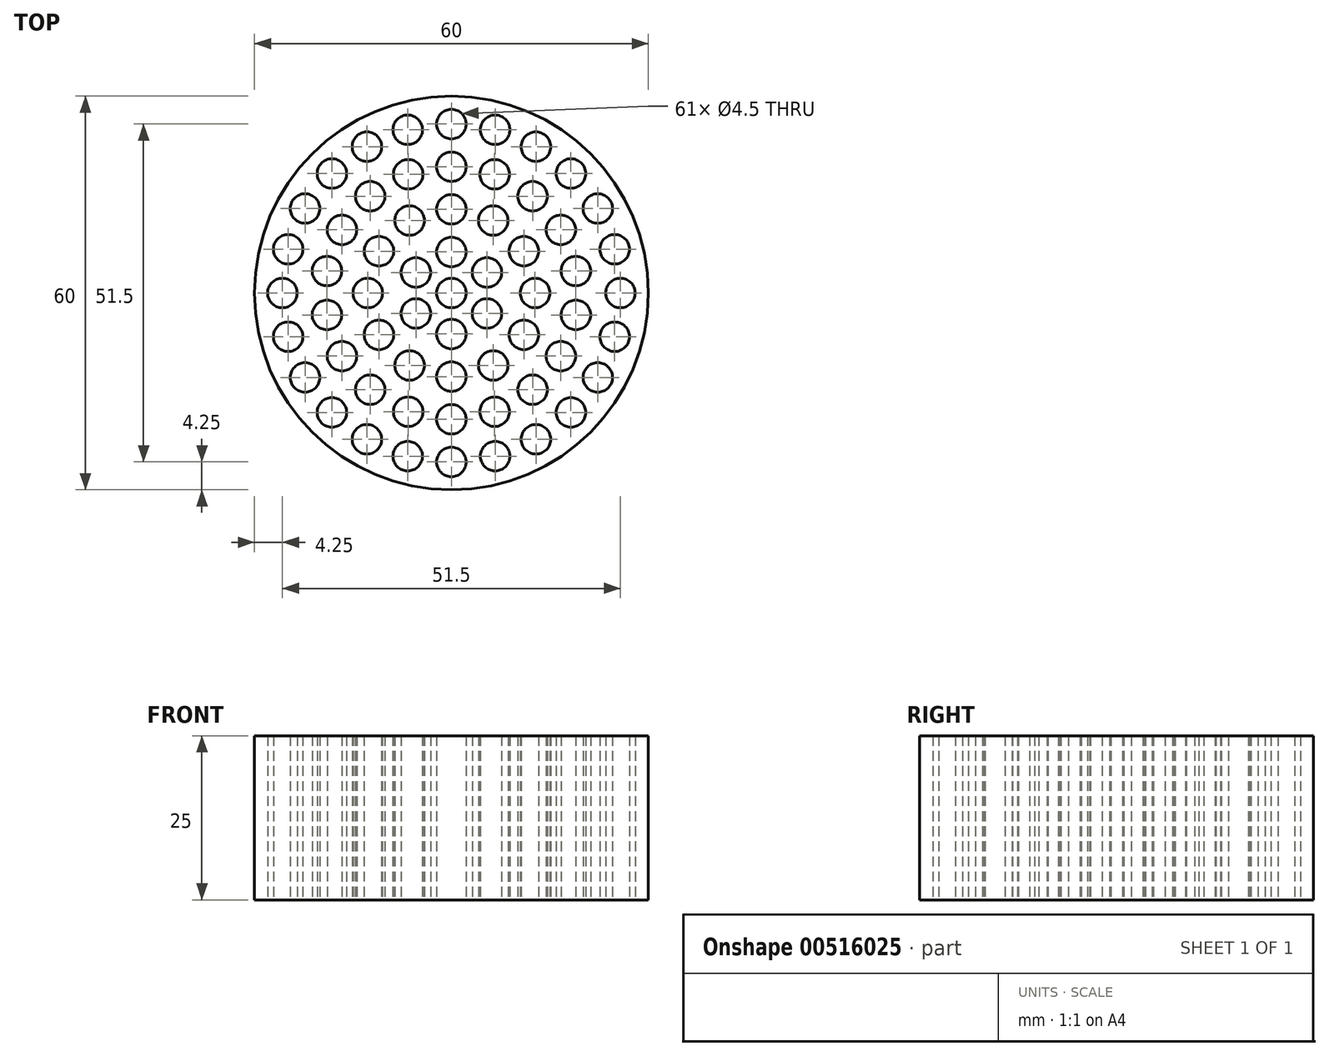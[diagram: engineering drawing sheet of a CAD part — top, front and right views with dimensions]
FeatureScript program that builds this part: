
annotation { "Feature Type Name" : "Feature", "Feature Type Description" : "" }
export const myFeature = defineFeature(function(context is Context, id is Id, definition is map)
    precondition{}
    {
        {
            var Q0;
            Q0=qCreatedBy(makeId("Top.planeOp"),FACE);
            var sketch = newSketch(context, id + "F0", { "sketchPlane" : qUnion([Q0])});
            skCircle(sketch, "E0", {"center": v(0, 0) * mm, "radius": 30 * mm});
            skLineSegment(sketch, "E1", {"start": v(0, 30) * mm, "end": v(0, -30) * mm});
            skCircle(sketch, "E2", {"center": v(0, 25.75) * mm, "radius": 2.25 * mm});
            skCircle(sketch, "E3.1.0", {"center": v(-6.66, 24.87) * mm, "radius": 2.25 * mm});
            skCircle(sketch, "E3.2.0", {"center": v(-12.87, 22.3) * mm, "radius": 2.25 * mm});
            skCircle(sketch, "E3.3.0", {"center": v(-18.2, 18.2) * mm, "radius": 2.25 * mm});
            skCircle(sketch, "E3.4.0", {"center": v(-22.3, 12.88) * mm, "radius": 2.25 * mm});
            skCircle(sketch, "E3.5.0", {"center": v(-24.87, 6.66) * mm, "radius": 2.25 * mm});
            skCircle(sketch, "E3.6.0", {"center": v(-25.75, 0) * mm, "radius": 2.25 * mm});
            skCircle(sketch, "E3.7.0", {"center": v(-24.87, -6.66) * mm, "radius": 2.25 * mm});
            skCircle(sketch, "E3.8.0", {"center": v(-22.3, -12.87) * mm, "radius": 2.25 * mm});
            skCircle(sketch, "E3.9.0", {"center": v(-18.2, -18.2) * mm, "radius": 2.25 * mm});
            skCircle(sketch, "E3.10.0", {"center": v(-12.87, -22.3) * mm, "radius": 2.25 * mm});
            skCircle(sketch, "E3.11.0", {"center": v(-6.66, -24.87) * mm, "radius": 2.25 * mm});
            skCircle(sketch, "E3.12.0", {"center": v(0, -25.75) * mm, "radius": 2.25 * mm});
            skCircle(sketch, "E3.13.0", {"center": v(6.66, -24.87) * mm, "radius": 2.25 * mm});
            skCircle(sketch, "E3.14.0", {"center": v(12.87, -22.3) * mm, "radius": 2.25 * mm});
            skCircle(sketch, "E3.15.0", {"center": v(18.2, -18.2) * mm, "radius": 2.25 * mm});
            skCircle(sketch, "E3.16.0", {"center": v(22.3, -12.88) * mm, "radius": 2.25 * mm});
            skCircle(sketch, "E3.17.0", {"center": v(24.87, -6.66) * mm, "radius": 2.25 * mm});
            skCircle(sketch, "E3.18.0", {"center": v(25.75, 0) * mm, "radius": 2.25 * mm});
            skCircle(sketch, "E3.19.0", {"center": v(24.87, 6.66) * mm, "radius": 2.25 * mm});
            skCircle(sketch, "E3.20.0", {"center": v(22.3, 12.88) * mm, "radius": 2.25 * mm});
            skCircle(sketch, "E3.21.0", {"center": v(18.2, 18.2) * mm, "radius": 2.25 * mm});
            skCircle(sketch, "E3.22.0", {"center": v(12.88, 22.3) * mm, "radius": 2.25 * mm});
            skCircle(sketch, "E3.23.0", {"center": v(6.66, 24.87) * mm, "radius": 2.25 * mm});
            skCircle(sketch, "E4", {"center": v(0, 19.25) * mm, "radius": 2.25 * mm});
            skCircle(sketch, "E5.1.0", {"center": v(-6.58, 18.09) * mm, "radius": 2.25 * mm});
            skCircle(sketch, "E5.2.0", {"center": v(-12.37, 14.75) * mm, "radius": 2.25 * mm});
            skCircle(sketch, "E5.3.0", {"center": v(-16.67, 9.63) * mm, "radius": 2.25 * mm});
            skCircle(sketch, "E5.4.0", {"center": v(-18.96, 3.34) * mm, "radius": 2.25 * mm});
            skCircle(sketch, "E5.5.0", {"center": v(-18.96, -3.34) * mm, "radius": 2.25 * mm});
            skCircle(sketch, "E5.6.0", {"center": v(-16.67, -9.62) * mm, "radius": 2.25 * mm});
            skCircle(sketch, "E5.7.0", {"center": v(-12.37, -14.75) * mm, "radius": 2.25 * mm});
            skCircle(sketch, "E5.8.0", {"center": v(-6.58, -18.09) * mm, "radius": 2.25 * mm});
            skCircle(sketch, "E5.9.0", {"center": v(0, -19.25) * mm, "radius": 2.25 * mm});
            skCircle(sketch, "E5.10.0", {"center": v(6.58, -18.09) * mm, "radius": 2.25 * mm});
            skCircle(sketch, "E5.11.0", {"center": v(12.37, -14.75) * mm, "radius": 2.25 * mm});
            skCircle(sketch, "E5.12.0", {"center": v(16.67, -9.63) * mm, "radius": 2.25 * mm});
            skCircle(sketch, "E5.13.0", {"center": v(18.96, -3.34) * mm, "radius": 2.25 * mm});
            skCircle(sketch, "E5.14.0", {"center": v(18.96, 3.34) * mm, "radius": 2.25 * mm});
            skCircle(sketch, "E5.15.0", {"center": v(16.67, 9.62) * mm, "radius": 2.25 * mm});
            skCircle(sketch, "E5.16.0", {"center": v(12.37, 14.75) * mm, "radius": 2.25 * mm});
            skCircle(sketch, "E5.17.0", {"center": v(6.58, 18.09) * mm, "radius": 2.25 * mm});
            skCircle(sketch, "E6", {"center": v(0, 12.75) * mm, "radius": 2.25 * mm});
            skPoint(sketch, "E6.centerSnap0", {"position": v(3.33, 12.44) * mm});
            skCircle(sketch, "E7.1.0", {"center": v(-6.37, 11.04) * mm, "radius": 2.25 * mm});
            skCircle(sketch, "E7.2.0", {"center": v(-11.04, 6.38) * mm, "radius": 2.25 * mm});
            skCircle(sketch, "E7.3.0", {"center": v(-12.75, 0) * mm, "radius": 2.25 * mm});
            skCircle(sketch, "E7.4.0", {"center": v(-11.04, -6.37) * mm, "radius": 2.25 * mm});
            skCircle(sketch, "E7.5.0", {"center": v(-6.37, -11.04) * mm, "radius": 2.25 * mm});
            skCircle(sketch, "E7.6.0", {"center": v(0, -12.75) * mm, "radius": 2.25 * mm});
            skCircle(sketch, "E7.7.0", {"center": v(6.37, -11.04) * mm, "radius": 2.25 * mm});
            skCircle(sketch, "E7.8.0", {"center": v(11.04, -6.38) * mm, "radius": 2.25 * mm});
            skCircle(sketch, "E7.9.0", {"center": v(12.75, 0) * mm, "radius": 2.25 * mm});
            skCircle(sketch, "E7.10.0", {"center": v(11.04, 6.37) * mm, "radius": 2.25 * mm});
            skCircle(sketch, "E7.11.0", {"center": v(6.38, 11.04) * mm, "radius": 2.25 * mm});
            skCircle(sketch, "E8", {"center": v(0, 6.25) * mm, "radius": 2.25 * mm});
            skCircle(sketch, "E9.1.0", {"center": v(-5.41, 3.13) * mm, "radius": 2.25 * mm});
            skCircle(sketch, "E9.2.0", {"center": v(-5.41, -3.12) * mm, "radius": 2.25 * mm});
            skCircle(sketch, "E9.3.0", {"center": v(0, -6.25) * mm, "radius": 2.25 * mm});
            skCircle(sketch, "E9.4.0", {"center": v(5.41, -3.13) * mm, "radius": 2.25 * mm});
            skCircle(sketch, "E9.5.0", {"center": v(5.41, 3.12) * mm, "radius": 2.25 * mm});
            skCircle(sketch, "E10", {"center": v(0, 0) * mm, "radius": 2.25 * mm});
            skSolve(sketch);
        }
        {
            var Q0;
            Q0=makeQuery(id+"F0.imprint","IMPRINT",FACE,{"disambiguationData":[TD([[makeQuery(id+"F0.imprint","IMPRINT",EDGE,{"derivedFrom":sQuery(id+"F0.wireOp",EDGE,"E3.13.0")}),-1.0]])]});
            var Q1;
            Q1=makeQuery(id+"F0.imprint","IMPRINT",FACE,{"disambiguationData":[TD([[makeQuery(id+"F0.imprint","IMPRINT",EDGE,{"derivedFrom":sQuery(id+"F0.wireOp",EDGE,"E3.1.0")}),-1.0]])]});
            extrude(context, id + "F1", {"entities" : qUnion([Q0, Q1]), "depth" : 25 * mm, "offsetDistance" : 25 * mm});
        }
    });
